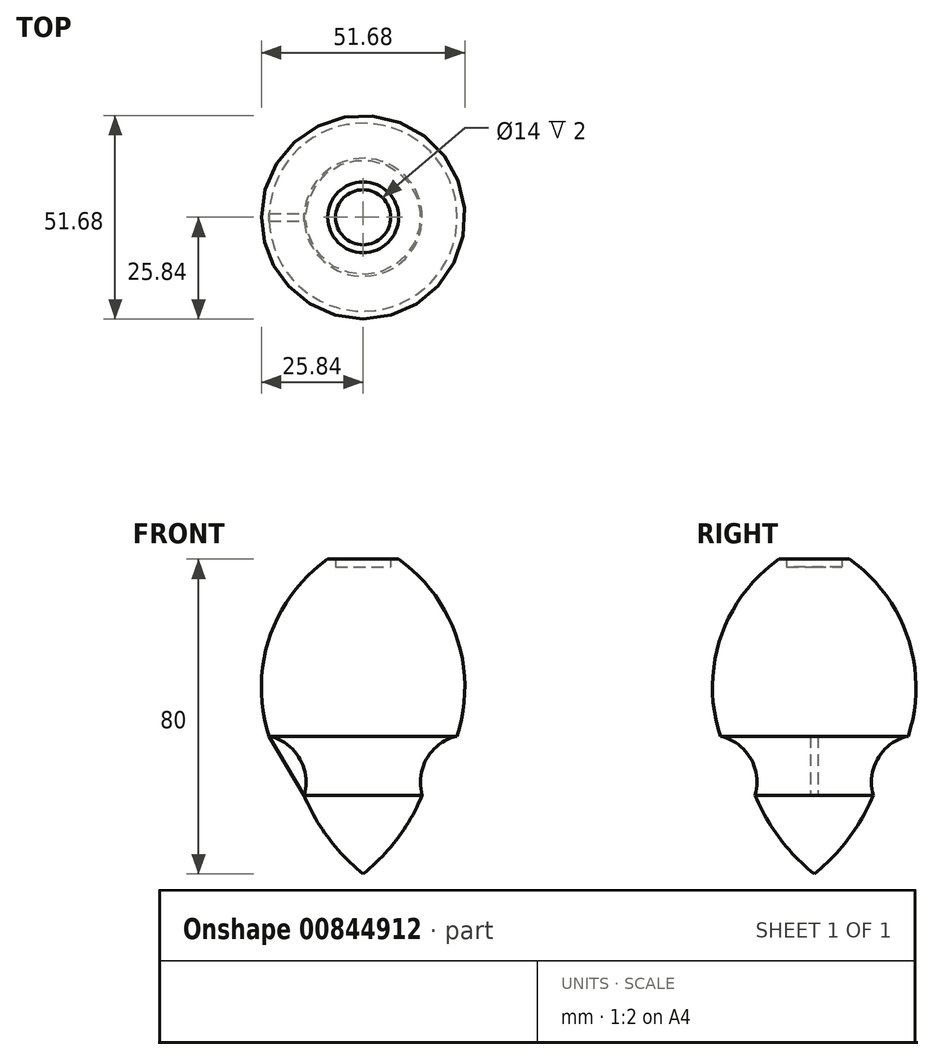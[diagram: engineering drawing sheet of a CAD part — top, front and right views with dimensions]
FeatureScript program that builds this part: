
annotation { "Feature Type Name" : "Feature", "Feature Type Description" : "" }
export const myFeature = defineFeature(function(context is Context, id is Id, definition is map)
    precondition{}
    {
        {
            var Q0;
            Q0=qCreatedBy(makeId("Front.planeOp"),FACE);
            var sketch = newSketch(context, id + "F0", { "sketchPlane" : qUnion([Q0])});
            skLineSegment(sketch, "E0", {"start": v(0, 0) * mm, "end": v(0, 80) * mm});
            skLineSegment(sketch, "E1", {"start": v(0, 80) * mm, "end": v(9, 80) * mm});
            skLineSegment(sketch, "E2", {"start": v(0, 35) * mm, "end": v(23.88, 35) * mm});
            skLineSegment(sketch, "E3", {"start": v(0, 20) * mm, "end": v(15, 20) * mm});
            skArc(sketch, "E4", {"start": v(23.88, 35) * mm, "mid": v(23.82, 59.94) * mm, "end": v(9, 80) * mm});
            skArc(sketch, "E5", {"start": v(23.88, 35) * mm, "mid": v(16.21, 29.41) * mm, "end": v(15, 20) * mm});
            skArc(sketch, "E6", {"start": v(0, 0) * mm, "mid": v(8.77, 9.05) * mm, "end": v(15, 20) * mm});
            skLineSegment(sketch, "E7", {"start": v(0, 78) * mm, "end": v(7, 78) * mm});
            skLineSegment(sketch, "E8", {"start": v(7, 78) * mm, "end": v(7, 80) * mm});
            skSolve(sketch);
        }
        {
            var Q0;
            {var subQ1=sQuery(id+"F0.wireOp",EDGE,"E2");Q0=makeQuery(id+"F0.imprint","IMPRINT",FACE,{"disambiguationData":[TD([[makeQuery(id+"F0.imprint","IMPRINT",EDGE,{"derivedFrom":subQ1}),1.0]])]});}
            var Q1;
            {var subQ0=sQuery(id+"F0.wireOp",EDGE,"E2");Q1=makeQuery(id+"F0.imprint","IMPRINT",FACE,{"disambiguationData":[TD([[makeQuery(id+"F0.imprint","IMPRINT",EDGE,{"derivedFrom":subQ0}),-1.0]])]});}
            var Q2;
            {var subQ2=sQuery(id+"F0.wireOp",EDGE,"E3");Q2=makeQuery(id+"F0.imprint","IMPRINT",FACE,{"disambiguationData":[TD([[makeQuery(id+"F0.imprint","IMPRINT",EDGE,{"derivedFrom":subQ2}),-1.0]])]});}
            var Q3;
            Q3=sQuery(id+"F0.wireOp",EDGE,"E0");
            revolve(context, id + "F1", {"surfaceOperationType" : NewSurfaceOperationType.NEW, "entities" : qUnion([Q0, Q1, Q2]), "axis" : qUnion([Q3]), "revolveType" : RevolveType.FULL});
        }
        {
            var Q0;
            Q0=qCreatedBy(makeId("Front.planeOp"),FACE);
            var sketch = newSketch(context, id + "F2", { "sketchPlane" : qUnion([Q0])});
            skLineSegment(sketch, "E9.0", {"start": v(23.88, 35) * mm, "end": v(-23.88, 35) * mm});
            skLineSegment(sketch, "E10.0", {"start": v(15, 20) * mm, "end": v(-15, 20) * mm});
            skLineSegment(sketch, "E11", {"start": v(-23.88, 35) * mm, "end": v(-15, 20) * mm});
            skLineSegment(sketch, "E12", {"start": v(0, 35) * mm, "end": v(0, 20) * mm});
            skSolve(sketch);
        }
        {
            var Q0;
            {var subQ0=sQuery(id+"F2.wireOp",EDGE,"E11");Q0=makeQuery(id+"F2.imprint","IMPRINT",FACE,{"disambiguationData":[TD([[makeQuery(id+"F2.imprint","IMPRINT",EDGE,{"derivedFrom":subQ0}),1.0]])]});}
            extrude(context, id + "F3", {"entities" : qUnion([Q0]), "operationType" : NewBodyOperationType.ADD, "endBound" : BoundingType.SYMMETRIC, "depth" : 2 * mm, "offsetDistance" : 25 * mm});
        }
    });
